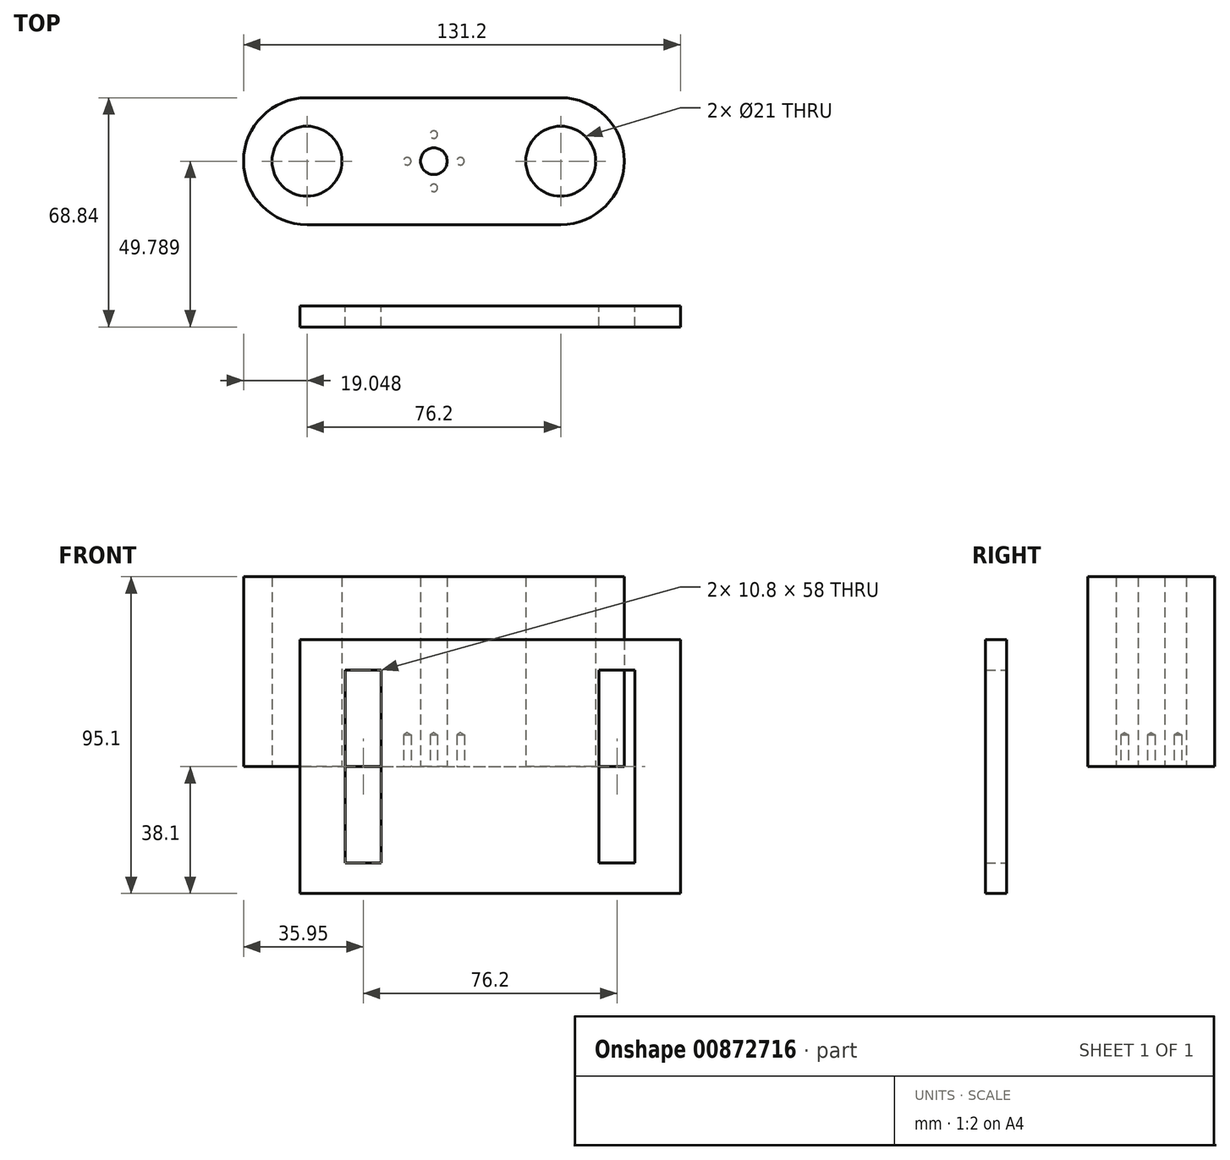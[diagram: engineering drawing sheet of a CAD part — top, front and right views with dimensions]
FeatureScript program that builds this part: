
annotation { "Feature Type Name" : "Feature", "Feature Type Description" : "" }
export const myFeature = defineFeature(function(context is Context, id is Id, definition is map)
    precondition{}
    {
        {
            var Q0;
            Q0=qCreatedBy(makeId("Front.planeOp"),FACE);
            var sketch = newSketch(context, id + "F0", { "sketchPlane" : qUnion([Q0])});
            skLineSegment(sketch, "E0.bottom", {"start": v(-57.15, 38.1) * mm, "end": v(57.15, 38.1) * mm});
            skLineSegment(sketch, "E0.top", {"start": v(-57.15, -38.1) * mm, "end": v(57.15, -38.1) * mm});
            skLineSegment(sketch, "E0.left", {"start": v(-57.15, 38.1) * mm, "end": v(-57.15, -38.1) * mm});
            skLineSegment(sketch, "E0.right", {"start": v(57.15, 38.1) * mm, "end": v(57.15, -38.1) * mm});
            skPoint(sketch, "E0.middle", {"position": v(0, 0) * mm});
            skLineSegment(sketch, "E1.bottom", {"start": v(-32.7, -29) * mm, "end": v(-43.5, -29) * mm});
            skLineSegment(sketch, "E1.top", {"start": v(-32.7, 29) * mm, "end": v(-43.5, 29) * mm});
            skLineSegment(sketch, "E1.left", {"start": v(-32.7, -29) * mm, "end": v(-32.7, 29) * mm});
            skLineSegment(sketch, "E1.right", {"start": v(-43.5, -29) * mm, "end": v(-43.5, 29) * mm});
            skPoint(sketch, "E1.middle", {"position": v(-38.1, 0) * mm});
            skLineSegment(sketch, "E2", {"start": v(0, 38.1) * mm, "end": v(0, -38.1) * mm, "construction": true});
            skLineSegment(sketch, "E3.MirrorCS", {"start": v(32.7, -29) * mm, "end": v(43.5, -29) * mm});
            skLineSegment(sketch, "E4.MirrorCS", {"start": v(32.7, 29) * mm, "end": v(43.5, 29) * mm});
            skLineSegment(sketch, "E5.MirrorCS", {"start": v(32.7, -29) * mm, "end": v(32.7, 29) * mm});
            skLineSegment(sketch, "E6.MirrorCS", {"start": v(43.5, -29) * mm, "end": v(43.5, 29) * mm});
            skPoint(sketch, "E7.MirrorP", {"position": v(38.1, 0) * mm});
            skSolve(sketch);
        }
        {
            var Q0;
            Q0=makeQuery(id+"F0.imprint","IMPRINT",FACE,{"disambiguationData":[TD([[makeQuery(id+"F0.imprint","IMPRINT",EDGE,{"derivedFrom":sQuery(id+"F0.wireOp",EDGE,"E0.bottom")}),-1.0]])]});
            extrude(context, id + "F1", {"entities" : qUnion([Q0]), "depth" : 6.35 * mm, "offsetDistance" : 25.4 * mm});
        }
        {
            var Q0;
            Q0=qCreatedBy(makeId("Top.planeOp"),FACE);
            var sketch = newSketch(context, id + "F2", { "sketchPlane" : qUnion([Q0])});
            skCircle(sketch, "E8", {"center": v(-55, 43.44) * mm, "radius": 10.5 * mm});
            skCircle(sketch, "E9", {"center": v(21.2, 43.44) * mm, "radius": 10.5 * mm});
            skLineSegment(sketch, "E10", {"start": v(-55, 43.44) * mm, "end": v(21.2, 43.44) * mm, "construction": true});
            skArc(sketch, "E11.0.startCap", {"start": v(-55, 24.39) * mm, "mid": v(-74.05, 43.44) * mm, "end": v(-55, 62.49) * mm});
            skArc(sketch, "E11.0.endCap", {"start": v(21.2, 62.49) * mm, "mid": v(40.25, 43.44) * mm, "end": v(21.2, 24.39) * mm});
            skLineSegment(sketch, "E11.0.left", {"start": v(-55, 62.49) * mm, "end": v(21.2, 62.49) * mm});
            skLineSegment(sketch, "E11.0.right", {"start": v(-55, 24.39) * mm, "end": v(21.2, 24.39) * mm});
            skCircle(sketch, "E12", {"center": v(-16.9, 43.44) * mm, "radius": 4 * mm});
            skLineSegment(sketch, "E13.top", {"start": v(-55, 14.86) * mm, "end": v(21.2, 14.86) * mm});
            skLineSegment(sketch, "E13.left", {"start": v(-55, 24.39) * mm, "end": v(-55, 14.86) * mm});
            skLineSegment(sketch, "E13.right", {"start": v(21.2, 24.39) * mm, "end": v(21.2, 14.86) * mm});
            skSolve(sketch);
        }
        {
            var Q0;
            Q0=makeQuery(id+"F2.imprint","IMPRINT",FACE,{"disambiguationData":[TD([[makeQuery(id+"F2.imprint","IMPRINT",EDGE,{"derivedFrom":sQuery(id+"F2.wireOp",EDGE,"E8")}),-1.0]])]});
            var Q1;
            Q1=makeQuery(id+"F2.imprint","IMPRINT",FACE,{"disambiguationData":[TD([[makeQuery(id+"F2.imprint","IMPRINT",EDGE,{"derivedFrom":sQuery(id+"F2.wireOp",EDGE,"E11.0.right")}),-1.0]])]});
            extrude(context, id + "F3", {"entities" : qUnion([Q0, Q1]), "depth" : 57 * mm, "offsetDistance" : 25.4 * mm});
        }
        {
            var Q0;
            Q0=makeQuery(id+"F3.opExtrude","CAP_FACE",FACE,{"disambiguationData":[OSD([sQuery(id+"F2.wireOp",EDGE,"E8"),sQuery(id+"F2.wireOp",EDGE,"E9"),sQuery(id+"F2.wireOp",EDGE,"E11.0.startCap"),sQuery(id+"F2.wireOp",EDGE,"E11.0.endCap"),sQuery(id+"F2.wireOp",EDGE,"E11.0.left"),sQuery(id+"F2.wireOp",EDGE,"E11.0.right"),sQuery(id+"F2.wireOp",EDGE,"E12")])],"isStart":true});
            var sketch = newSketch(context, id + "F4", { "sketchPlane" : qUnion([Q0])});
            skPoint(sketch, "E14", {"position": v(-16.9, -43.44) * mm});
            skCircle(sketch, "E15", {"center": v(-24.9, -43.44) * mm, "radius": 1.75 * mm});
            skCircle(sketch, "E16.1.0", {"center": v(-16.9, -51.44) * mm, "radius": 1.75 * mm});
            skCircle(sketch, "E16.2.0", {"center": v(-8.9, -43.44) * mm, "radius": 1.75 * mm});
            skCircle(sketch, "E16.3.0", {"center": v(-16.9, -35.44) * mm, "radius": 1.75 * mm});
            skSolve(sketch);
        }
        {
            var Q0;
            Q0=sQuery(id+"F4.wireOp",VERTEX,"E15.center");
            var Q1;
            Q1=sQuery(id+"F4.wireOp",VERTEX,"E16.3.0.center");
            var Q2;
            Q2=sQuery(id+"F4.wireOp",VERTEX,"E16.2.0.center");
            var Q3;
            Q3=sQuery(id+"F4.wireOp",VERTEX,"E16.1.0.center");
            var Q4;
            Q4=makeQuery(id+"F3.opExtrude","SWEPT_BODY",BODY,{"disambiguationData":[OSD([sQuery(id+"F2.wireOp",EDGE,"E8"),sQuery(id+"F2.wireOp",EDGE,"E9"),sQuery(id+"F2.wireOp",EDGE,"E11.0.startCap"),sQuery(id+"F2.wireOp",EDGE,"E11.0.endCap"),sQuery(id+"F2.wireOp",EDGE,"E11.0.left"),sQuery(id+"F2.wireOp",EDGE,"E11.0.right"),sQuery(id+"F2.wireOp",EDGE,"E12")])]});
            hole(context, id + "F5", {"style" : HoleStyle.SIMPLE, "endStyle" : HoleEndStyle.BLIND, "standardTappedOrClearance" : lookupTablePath({ "standard" : "ANSI", "engagement" : "75%", "pitch" : "40 tpi", "size" : "#4", "type" : "Tapped" }), "standardBlindInLast" : lookupTablePath({ "standard" : "ANSI", "engagement" : "75%", "pitch" : "40 tpi", "size" : "#4", "type" : "Tapped" }), "holeDiameter" : 2.26 * mm, "majorDiameter" : 2.84 * mm, "showTappedDepth" : true, "holeDepth" : 9.52 * mm, "isTappedThrough" : true, "tappedDepth" : 7.62 * mm, "tapClearance" : 3, "locations" : qUnion([Q0, Q1, Q2, Q3]), "scope" : qUnion([Q4])});
        }
    });
